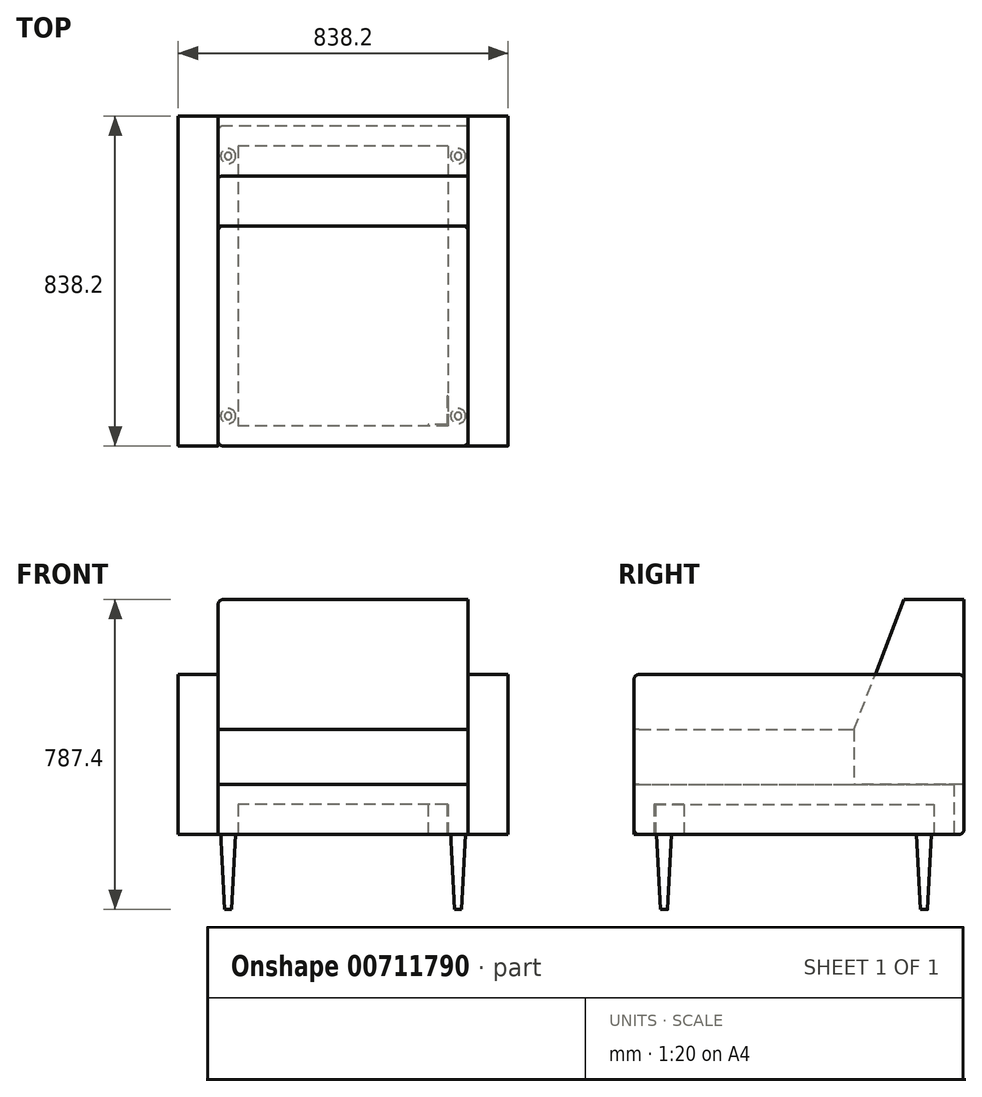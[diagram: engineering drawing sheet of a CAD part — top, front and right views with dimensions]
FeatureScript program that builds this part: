
annotation { "Feature Type Name" : "Feature", "Feature Type Description" : "" }
export const myFeature = defineFeature(function(context is Context, id is Id, definition is map)
    precondition{}
    {
        {
            var Q0;
            Q0=qCreatedBy(makeId("Right.planeOp"),FACE);
            var sketch = newSketch(context, id + "F0", { "sketchPlane" : qUnion([Q0])});
            skLineSegment(sketch, "E0.bottom", {"start": v(0, 596.9) * mm, "end": v(-838.2, 596.9) * mm});
            skLineSegment(sketch, "E0.top", {"start": v(0, 190.5) * mm, "end": v(-838.2, 190.5) * mm});
            skLineSegment(sketch, "E0.left", {"start": v(0, 596.9) * mm, "end": v(0, 190.5) * mm});
            skLineSegment(sketch, "E0.right", {"start": v(-838.2, 596.9) * mm, "end": v(-838.2, 190.5) * mm});
            skSolve(sketch);
        }
        {
            var Q0;
            Q0 = qSketchRegion(id + "F0", true);
            extrude(context, id + "F1", {"entities" : qUnion([Q0]), "oppositeDirection" : true, "depth" : 101.6 * mm, "offsetDistance" : 25.4 * mm});
        }
        {
            var Q0;
            Q0=makeQuery(id+"F1.opExtrude","CAP_FACE",FACE,{"disambiguationData":[OSD([sQuery(id+"F0.wireOp",EDGE,"E0.bottom"),sQuery(id+"F0.wireOp",EDGE,"E0.top"),sQuery(id+"F0.wireOp",EDGE,"E0.left"),sQuery(id+"F0.wireOp",EDGE,"E0.right")])],"isStart":true});
            var sketch = newSketch(context, id + "F2", { "sketchPlane" : qUnion([Q0])});
            skLineSegment(sketch, "E1.bottom", {"start": v(-838.2, 457.2) * mm, "end": v(-279.4, 457.2) * mm});
            skLineSegment(sketch, "E1.top", {"start": v(-838.2, 317.5) * mm, "end": v(-279.4, 317.5) * mm});
            skLineSegment(sketch, "E1.left", {"start": v(-838.2, 457.2) * mm, "end": v(-838.2, 317.5) * mm});
            skLineSegment(sketch, "E1.right", {"start": v(-279.4, 457.2) * mm, "end": v(-279.4, 317.5) * mm});
            skSolve(sketch);
        }
        {
            var Q0;
            Q0 = qSketchRegion(id + "F2", true);
            extrude(context, id + "F3", {"entities" : qUnion([Q0]), "depth" : 635 * mm, "offsetDistance" : 25.4 * mm});
        }
        {
            var Q0;
            Q0=makeQuery(id+"F1.opExtrude","CAP_FACE",FACE,{"disambiguationData":[OSD([sQuery(id+"F0.wireOp",EDGE,"E0.bottom"),sQuery(id+"F0.wireOp",EDGE,"E0.top"),sQuery(id+"F0.wireOp",EDGE,"E0.left"),sQuery(id+"F0.wireOp",EDGE,"E0.right")])],"isStart":true});
            var sketch = newSketch(context, id + "F4", { "sketchPlane" : qUnion([Q0])});
            skLineSegment(sketch, "E2.bottom", {"start": v(-838.2, 317.5) * mm, "end": v(-25.4, 317.5) * mm});
            skLineSegment(sketch, "E2.top", {"start": v(-838.2, 190.5) * mm, "end": v(-25.4, 190.5) * mm});
            skLineSegment(sketch, "E2.left", {"start": v(-838.2, 317.5) * mm, "end": v(-838.2, 190.5) * mm});
            skLineSegment(sketch, "E2.right", {"start": v(-25.4, 317.5) * mm, "end": v(-25.4, 190.5) * mm});
            skSolve(sketch);
        }
        {
            var Q0;
            Q0 = qSketchRegion(id + "F4", true);
            var Q1;
            Q1=makeQuery(id+"F3.opExtrude","CAP_FACE",FACE,{"disambiguationData":[OSD([sQuery(id+"F2.wireOp",EDGE,"E1.bottom"),sQuery(id+"F2.wireOp",EDGE,"E1.top"),sQuery(id+"F2.wireOp",EDGE,"E1.left"),sQuery(id+"F2.wireOp",EDGE,"E1.right")])],"isStart":false});
            extrude(context, id + "F5", {"entities" : qUnion([Q0]), "endBound" : BoundingType.UP_TO_SURFACE, "depth" : 25.4 * mm, "endBoundEntityFace" : qUnion([Q1]), "offsetDistance" : 25.4 * mm});
        }
        {
            var Q0;
            Q0=qCreatedBy(makeId("Right.planeOp"),FACE);
            var sketch = newSketch(context, id + "F6", { "sketchPlane" : qUnion([Q0])});
            skLineSegment(sketch, "E3", {"start": v(-279.4, 457.2) * mm, "end": v(-152.4, 787.4) * mm});
            skLineSegment(sketch, "E4", {"start": v(-152.4, 787.4) * mm, "end": v(0, 787.4) * mm});
            skLineSegment(sketch, "E5", {"start": v(0, 787.4) * mm, "end": v(0, 317.5) * mm});
            skLineSegment(sketch, "E6", {"start": v(0, 317.5) * mm, "end": v(-279.4, 317.5) * mm});
            skLineSegment(sketch, "E7", {"start": v(-279.4, 317.5) * mm, "end": v(-279.4, 457.2) * mm});
            skSolve(sketch);
        }
        {
            var Q0;
            Q0 = qSketchRegion(id + "F6", true);
            var Q1;
            Q1=makeQuery(id+"F3.opExtrude","CAP_FACE",FACE,{"disambiguationData":[OSD([sQuery(id+"F2.wireOp",EDGE,"E1.bottom"),sQuery(id+"F2.wireOp",EDGE,"E1.top"),sQuery(id+"F2.wireOp",EDGE,"E1.left"),sQuery(id+"F2.wireOp",EDGE,"E1.right")])],"isStart":false});
            extrude(context, id + "F7", {"entities" : qUnion([Q0]), "endBound" : BoundingType.UP_TO_SURFACE, "depth" : 25.4 * mm, "endBoundEntityFace" : qUnion([Q1]), "offsetDistance" : 25.4 * mm});
        }
        {
            var Q0;
            Q0=makeQuery(id+"F3.opExtrude","CAP_FACE",FACE,{"disambiguationData":[OSD([sQuery(id+"F2.wireOp",EDGE,"E1.bottom"),sQuery(id+"F2.wireOp",EDGE,"E1.top"),sQuery(id+"F2.wireOp",EDGE,"E1.left"),sQuery(id+"F2.wireOp",EDGE,"E1.right")])],"isStart":false});
            var sketch = newSketch(context, id + "F8", { "sketchPlane" : qUnion([Q0])});
            skLineSegment(sketch, "E8.0.0", {"start": v(0, 190.5) * mm, "end": v(-838.2, 190.5) * mm});
            skLineSegment(sketch, "E8.0.1", {"start": v(-838.2, 190.5) * mm, "end": v(-838.2, 596.9) * mm});
            skLineSegment(sketch, "E8.0.2", {"start": v(-838.2, 596.9) * mm, "end": v(0, 596.9) * mm});
            skLineSegment(sketch, "E8.0.3", {"start": v(0, 596.9) * mm, "end": v(0, 190.5) * mm});
            skSolve(sketch);
        }
        {
            var Q0;
            Q0 = qSketchRegion(id + "F8", true);
            extrude(context, id + "F9", {"entities" : qUnion([Q0]), "depth" : 101.6 * mm, "offsetDistance" : 25.4 * mm});
        }
        {
            var Q0;
            Q0=makeQuery(id+"F5.opExtrude","SWEPT_FACE",FACE,{"disambiguationData":[OSD([sQuery(id+"F4.wireOp",EDGE,"E2.top")])]});
            shell(context, id + "F10", {"entities" : qUnion([Q0]), "thickness" : 50.8 * mm});
        }
        {
            var Q0;
            Q0=makeQuery(id+"F5.opExtrude","SWEPT_FACE",FACE,{"disambiguationData":[OSD([sQuery(id+"F4.wireOp",EDGE,"E2.top")])]});
            var sketch = newSketch(context, id + "F11", { "sketchPlane" : qUnion([Q0])});
            skCircle(sketch, "E9", {"center": v(25.4, 762) * mm, "radius": 19.05 * mm});
            skCircle(sketch, "E10", {"center": v(609.6, 762) * mm, "radius": 19.05 * mm});
            skLineSegment(sketch, "E11", {"start": v(50.8, 101.6) * mm, "end": v(0, 101.6) * mm, "construction": true});
            skLineSegment(sketch, "E12", {"start": v(584.2, 101.6) * mm, "end": v(635, 101.6) * mm, "construction": true});
            skCircle(sketch, "E13", {"center": v(25.4, 101.6) * mm, "radius": 19.05 * mm});
            skCircle(sketch, "E14", {"center": v(609.6, 101.6) * mm, "radius": 19.05 * mm});
            skLineSegment(sketch, "E15", {"start": v(584.2, 762) * mm, "end": v(635, 762) * mm, "construction": true});
            skLineSegment(sketch, "E16", {"start": v(0, 762) * mm, "end": v(50.8, 762) * mm, "construction": true});
            skSolve(sketch);
        }
        {
            var Q0;
            Q0 = qSketchRegion(id + "F11", true);
            var Q1;
            Q1=qCreatedBy(makeId("Top.planeOp"),FACE);
            extrude(context, id + "F12", {"entities" : qUnion([Q0]), "endBound" : BoundingType.UP_TO_SURFACE, "depth" : 25.4 * mm, "endBoundEntityFace" : qUnion([Q1]), "offsetDistance" : 25.4 * mm, "hasDraft" : true, "draftAngle" : 3 * degree, "draftPullDirection" : true});
        }
        {
            var Q0;
            Q0=makeQuery(id+"F1.opExtrude","SWEPT_EDGE",EDGE,{"disambiguationData":[OSD([sQuery(id+"F0.wireOp",EDGE,"E0.bottom"),sQuery(id+"F0.wireOp",EDGE,"E0.right")])]});
            var Q1;
            Q1=makeQuery(id+"F1.opExtrude","SWEPT_EDGE",EDGE,{"disambiguationData":[OSD([sQuery(id+"F0.wireOp",EDGE,"E0.top"),sQuery(id+"F0.wireOp",EDGE,"E0.right")])]});
            var Q2;
            Q2=makeQuery(id+"F9.opExtrude","SWEPT_EDGE",EDGE,{"disambiguationData":[OSD([sQuery(id+"F8.wireOp",EDGE,"E8.0.1"),sQuery(id+"F8.wireOp",EDGE,"E8.0.2")])]});
            var Q3;
            Q3=makeQuery(id+"F9.opExtrude","SWEPT_EDGE",EDGE,{"disambiguationData":[OSD([sQuery(id+"F8.wireOp",EDGE,"E8.0.2"),sQuery(id+"F8.wireOp",EDGE,"E8.0.3")])]});
            var Q4;
            Q4=makeQuery(id+"F9.opExtrude","SWEPT_EDGE",EDGE,{"disambiguationData":[OSD([sQuery(id+"F8.wireOp",EDGE,"E8.0.0"),sQuery(id+"F8.wireOp",EDGE,"E8.0.1")])]});
            var Q5;
            Q5=makeQuery(id+"F3.opExtrude","CAP_EDGE",EDGE,{"disambiguationData":[OSD([sQuery(id+"F2.wireOp",EDGE,"E1.left")])],"isStart":false});
            var Q6;
            Q6=makeQuery(id+"F5.opExtrude","TWEAK_EDGE",EDGE,{"derivedFrom":[makeQuery(id+"F3.opExtrude","CAP_FACE",FACE,{"disambiguationData":[OSD([sQuery(id+"F2.wireOp",EDGE,"E1.bottom"),sQuery(id+"F2.wireOp",EDGE,"E1.top"),sQuery(id+"F2.wireOp",EDGE,"E1.left"),sQuery(id+"F2.wireOp",EDGE,"E1.right")])],"isStart":false}),makeQuery(id+"F4.imprint","IMPRINT",EDGE,{"derivedFrom":sQuery(id+"F4.wireOp",EDGE,"E2.left")})]});
            var Q7;
            Q7=makeQuery(id+"F3.opExtrude","CAP_EDGE",EDGE,{"disambiguationData":[OSD([sQuery(id+"F2.wireOp",EDGE,"E1.left")])],"isStart":true});
            var Q8;
            Q8=makeQuery(id+"F5.opExtrude","CAP_EDGE",EDGE,{"disambiguationData":[OSD([sQuery(id+"F4.wireOp",EDGE,"E2.left")])],"isStart":true});
            var Q9;
            Q9=makeQuery(id+"F9.opExtrude","SWEPT_EDGE",EDGE,{"disambiguationData":[OSD([sQuery(id+"F8.wireOp",EDGE,"E8.0.0"),sQuery(id+"F8.wireOp",EDGE,"E8.0.3")])]});
            var Q10;
            Q10=makeQuery(id+"F1.opExtrude","SWEPT_EDGE",EDGE,{"disambiguationData":[OSD([sQuery(id+"F0.wireOp",EDGE,"E0.top"),sQuery(id+"F0.wireOp",EDGE,"E0.left")])]});
            var Q11;
            Q11=makeQuery(id+"F1.opExtrude","SWEPT_EDGE",EDGE,{"disambiguationData":[OSD([sQuery(id+"F0.wireOp",EDGE,"E0.bottom"),sQuery(id+"F0.wireOp",EDGE,"E0.left")])]});
            var Q12;
            Q12=makeQuery(id+"F7.opExtrude","TWEAK_EDGE",EDGE,{"derivedFrom":[makeQuery(id+"F3.opExtrude","CAP_FACE",FACE,{"disambiguationData":[OSD([sQuery(id+"F2.wireOp",EDGE,"E1.bottom"),sQuery(id+"F2.wireOp",EDGE,"E1.top"),sQuery(id+"F2.wireOp",EDGE,"E1.left"),sQuery(id+"F2.wireOp",EDGE,"E1.right")])],"isStart":false}),makeQuery(id+"F6.imprint","IMPRINT",EDGE,{"derivedFrom":sQuery(id+"F6.wireOp",EDGE,"E4")})]});
            var Q13;
            Q13=makeQuery(id+"F7.opExtrude","CAP_EDGE",EDGE,{"disambiguationData":[OSD([sQuery(id+"F6.wireOp",EDGE,"E4")])],"isStart":true});
            var Q14;
            Q14=makeQuery(id+"F3.opExtrude","CAP_EDGE",EDGE,{"disambiguationData":[OSD([sQuery(id+"F2.wireOp",EDGE,"E1.right")])],"isStart":true});
            var Q15;
            Q15=makeQuery(id+"F5.opExtrude","CAP_EDGE",EDGE,{"disambiguationData":[OSD([sQuery(id+"F4.wireOp",EDGE,"E2.right")])],"isStart":true});
            var Q16;
            Q16=makeQuery(id+"F3.opExtrude","CAP_EDGE",EDGE,{"disambiguationData":[OSD([sQuery(id+"F2.wireOp",EDGE,"E1.right")])],"isStart":false});
            var Q17;
            Q17=makeQuery(id+"F5.opExtrude","TWEAK_EDGE",EDGE,{"derivedFrom":[makeQuery(id+"F3.opExtrude","CAP_FACE",FACE,{"disambiguationData":[OSD([sQuery(id+"F2.wireOp",EDGE,"E1.bottom"),sQuery(id+"F2.wireOp",EDGE,"E1.top"),sQuery(id+"F2.wireOp",EDGE,"E1.left"),sQuery(id+"F2.wireOp",EDGE,"E1.right")])],"isStart":false}),makeQuery(id+"F4.imprint","IMPRINT",EDGE,{"derivedFrom":sQuery(id+"F4.wireOp",EDGE,"E2.right")})]});
            fillet(context, id + "F13", {"entities" : qUnion([Q0, Q1, Q2, Q3, Q4, Q5, Q6, Q7, Q8, Q9, Q10, Q11, Q12, Q13, Q14, Q15, Q16, Q17]), "radius" : 12.7 * mm, "tangentPropagation" : true, "allowEdgeOverflow" : false});
        }
        {
            var Q0;
            Q0=makeQuery(id+"F5.opExtrude","SWEPT_FACE",FACE,{"disambiguationData":[OSD([sQuery(id+"F4.wireOp",EDGE,"E2.top")])]});
            var sketch = newSketch(context, id + "F14", { "sketchPlane" : qUnion([Q0])});
            skLineSegment(sketch, "E17", {"start": v(584.2, 787.4) * mm, "end": v(584.2, 711.2) * mm});
            skLineSegment(sketch, "E18", {"start": v(584.2, 711.2) * mm, "end": v(581.03, 711.2) * mm});
            skLineSegment(sketch, "E19", {"start": v(581.03, 711.2) * mm, "end": v(581.03, 784.23) * mm});
            skLineSegment(sketch, "E20", {"start": v(581.03, 784.23) * mm, "end": v(533.4, 784.23) * mm});
            skLineSegment(sketch, "E21", {"start": v(533.4, 784.23) * mm, "end": v(533.4, 787.4) * mm});
            skLineSegment(sketch, "E22", {"start": v(533.4, 787.4) * mm, "end": v(584.2, 787.4) * mm});
            skSolve(sketch);
        }
        {
            var Q0;
            Q0 = qSketchRegion(id + "F14", true);
            var Q1;
            Q1=makeQuery(id+"F10.opShell","OFFSET_FACE",FACE,{"disambiguationData":[OSD([sQuery(id+"F4.wireOp",EDGE,"E2.bottom")])]});
            extrude(context, id + "F15", {"entities" : qUnion([Q0]), "endBound" : BoundingType.UP_TO_SURFACE, "oppositeDirection" : true, "depth" : 25.4 * mm, "endBoundEntityFace" : qUnion([Q1]), "offsetDistance" : 25.4 * mm});
        }
    });
